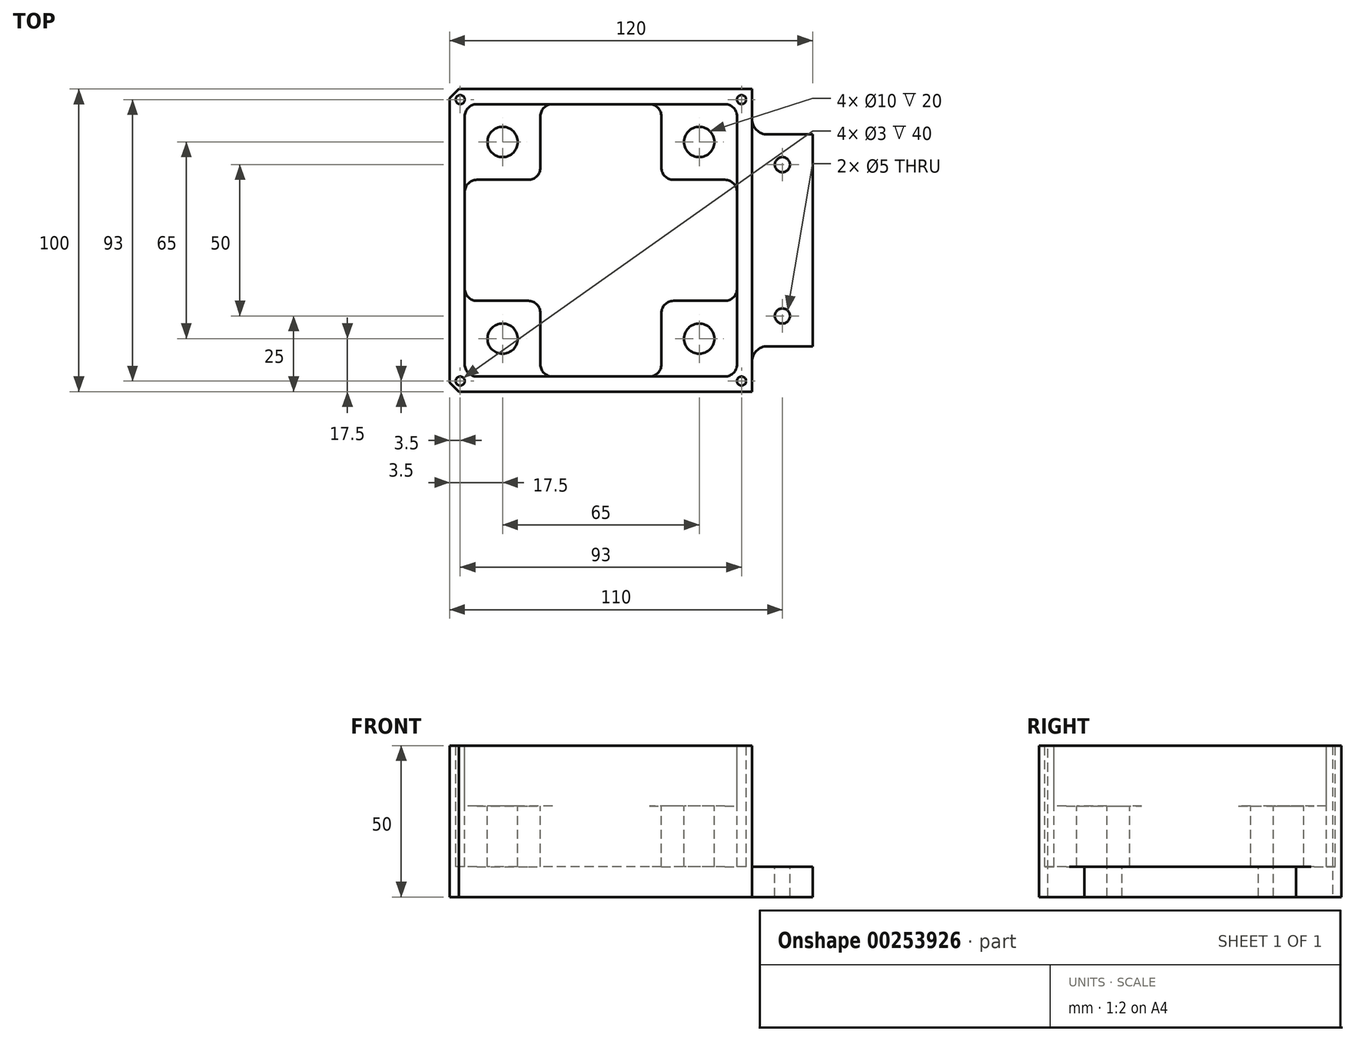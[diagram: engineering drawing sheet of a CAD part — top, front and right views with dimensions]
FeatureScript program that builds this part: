
annotation { "Feature Type Name" : "Feature", "Feature Type Description" : "" }
export const myFeature = defineFeature(function(context is Context, id is Id, definition is map)
    precondition{}
    {
        {
            var Q0;
            Q0=qCreatedBy(makeId("Top.planeOp"),FACE);
            var sketch = newSketch(context, id + "F0", { "sketchPlane" : qUnion([Q0])});
            skLineSegment(sketch, "E0.bottom", {"start": v(50, -50) * mm, "end": v(-50, -50) * mm});
            skLineSegment(sketch, "E0.top", {"start": v(50, 50) * mm, "end": v(-50, 50) * mm});
            skLineSegment(sketch, "E0.right", {"start": v(-50, -50) * mm, "end": v(-50, 50) * mm});
            skPoint(sketch, "E0.middle", {"position": v(0, 0) * mm});
            skLineSegment(sketch, "E1", {"start": v(50, 50) * mm, "end": v(70, 50) * mm});
            skLineSegment(sketch, "E2", {"start": v(70, 50) * mm, "end": v(70, -50) * mm});
            skLineSegment(sketch, "E3", {"start": v(70, -50) * mm, "end": v(50, -50) * mm});
            skSolve(sketch);
        }
        {
            var Q0;
            Q0=makeQuery(id+"F0.imprint","IMPRINT",FACE,{"disambiguationData":[TD([[makeQuery(id+"F0.imprint","IMPRINT",EDGE,{"derivedFrom":sQuery(id+"F0.wireOp",EDGE,"E0.bottom")}),-1.0]])]});
            extrude(context, id + "F1", {"entities" : qUnion([Q0]), "depth" : 50 * mm});
        }
        {
            var Q0;
            Q0=makeQuery(id+"F1.opExtrude","CAP_FACE",FACE,{"disambiguationData":[OSD([sQuery(id+"F0.wireOp",EDGE,"E0.bottom"),sQuery(id+"F0.wireOp",EDGE,"E0.top"),sQuery(id+"F0.wireOp",EDGE,"E0.right"),sQuery(id+"F0.wireOp",EDGE,"E1"),sQuery(id+"F0.wireOp",EDGE,"E2"),sQuery(id+"F0.wireOp",EDGE,"E3")])],"isStart":false});
            var sketch = newSketch(context, id + "F2", { "sketchPlane" : qUnion([Q0])});
            skLineSegment(sketch, "E4.bottom", {"start": v(70, 50) * mm, "end": v(50, 50) * mm});
            skLineSegment(sketch, "E4.top", {"start": v(70, -50) * mm, "end": v(50, -50) * mm});
            skLineSegment(sketch, "E4.left", {"start": v(70, 50) * mm, "end": v(70, -50) * mm});
            skLineSegment(sketch, "E4.right", {"start": v(50, 50) * mm, "end": v(50, -50) * mm});
            skSolve(sketch);
        }
        {
            var Q0;
            Q0=qSketchRegion(id+"F2",true);
            extrude(context, id + "F3", {"entities" : qUnion([Q0]), "operationType" : NewBodyOperationType.REMOVE, "oppositeDirection" : true, "depth" : 40 * mm});
        }
        {
            var Q0;
            Q0=makeQuery(id+"F3.boolean.opBoolean","COPY",FACE,{"derivedFrom":makeQuery(id+"F3.opExtrude","CAP_FACE",FACE,{"disambiguationData":[OSD([sQuery(id+"F2.wireOp",EDGE,"E4.bottom"),sQuery(id+"F2.wireOp",EDGE,"E4.top"),sQuery(id+"F2.wireOp",EDGE,"E4.left"),sQuery(id+"F2.wireOp",EDGE,"E4.right")])],"isStart":false})});
            var sketch = newSketch(context, id + "F4", { "sketchPlane" : qUnion([Q0])});
            skLineSegment(sketch, "E5.bottom", {"start": v(50, -50) * mm, "end": v(70, -50) * mm});
            skLineSegment(sketch, "E5.top", {"start": v(55, -35) * mm, "end": v(70, -35) * mm});
            skLineSegment(sketch, "E5.left", {"start": v(50, -50) * mm, "end": v(50, -40) * mm});
            skLineSegment(sketch, "E5.right", {"start": v(70, -50) * mm, "end": v(70, -35) * mm});
            skPoint(sketch, "E6.visualSharp", {"position": v(50, -35) * mm});
            skArc(sketch, "E6.filletArc", {"start": v(55, -35) * mm, "mid": v(51.46, -36.46) * mm, "end": v(50, -40) * mm});
            skCircle(sketch, "E7", {"center": v(60, -25) * mm, "radius": 2.5 * mm});
            skPoint(sketch, "E8.MirrorP", {"position": v(50, 35) * mm});
            skCircle(sketch, "E9.MirrorC", {"center": v(60, 25) * mm, "radius": 2.5 * mm});
            skArc(sketch, "E10.MirrorCS", {"start": v(55, 35) * mm, "mid": v(51.46, 36.46) * mm, "end": v(50, 40) * mm});
            skLineSegment(sketch, "E11.MirrorCS", {"start": v(70, 50) * mm, "end": v(70, 35) * mm});
            skLineSegment(sketch, "E12.MirrorCS", {"start": v(50, 50) * mm, "end": v(50, 40) * mm});
            skLineSegment(sketch, "E13.MirrorCS", {"start": v(50, 50) * mm, "end": v(70, 50) * mm});
            skLineSegment(sketch, "E14.MirrorCS", {"start": v(55, 35) * mm, "end": v(70, 35) * mm});
            skSolve(sketch);
        }
        {
            var Q0;
            Q0=qSketchRegion(id+"F4",true);
            extrude(context, id + "F5", {"entities" : qUnion([Q0]), "operationType" : NewBodyOperationType.REMOVE, "endBound" : BoundingType.UP_TO_NEXT, "oppositeDirection" : true, "depth" : 25 * mm});
        }
        {
            var Q0;
            Q0=makeQuery(id+"F1.opExtrude","CAP_FACE",FACE,{"disambiguationData":[OSD([sQuery(id+"F0.wireOp",EDGE,"E0.bottom"),sQuery(id+"F0.wireOp",EDGE,"E0.top"),sQuery(id+"F0.wireOp",EDGE,"E0.right"),sQuery(id+"F0.wireOp",EDGE,"E1"),sQuery(id+"F0.wireOp",EDGE,"E2"),sQuery(id+"F0.wireOp",EDGE,"E3")])],"isStart":false});
            var sketch = newSketch(context, id + "F6", { "sketchPlane" : qUnion([Q0])});
            skLineSegment(sketch, "E15.bottom", {"start": v(45, -45) * mm, "end": v(-45, -45) * mm});
            skLineSegment(sketch, "E15.top", {"start": v(45, 45) * mm, "end": v(-45, 45) * mm});
            skLineSegment(sketch, "E15.left", {"start": v(45, -45) * mm, "end": v(45, 45) * mm});
            skLineSegment(sketch, "E15.right", {"start": v(-45, -45) * mm, "end": v(-45, 45) * mm});
            skPoint(sketch, "E15.middle", {"position": v(0, 0) * mm});
            skSolve(sketch);
        }
        {
            var Q0;
            Q0=qSketchRegion(id+"F6",true);
            extrude(context, id + "F7", {"entities" : qUnion([Q0]), "operationType" : NewBodyOperationType.REMOVE, "oppositeDirection" : true, "depth" : 20 * mm});
        }
        {
            var Q0;
            Q0=makeQuery(id+"F7.boolean.opBoolean","COPY",FACE,{"derivedFrom":makeQuery(id+"F7.opExtrude","CAP_FACE",FACE,{"disambiguationData":[OSD([sQuery(id+"F6.wireOp",EDGE,"E15.bottom"),sQuery(id+"F6.wireOp",EDGE,"E15.top"),sQuery(id+"F6.wireOp",EDGE,"E15.left"),sQuery(id+"F6.wireOp",EDGE,"E15.right")])],"isStart":false})});
            var sketch = newSketch(context, id + "F8", { "sketchPlane" : qUnion([Q0])});
            skCircle(sketch, "E16", {"center": v(-32.5, 32.5) * mm, "radius": 5 * mm});
            skLineSegment(sketch, "E17.0", {"start": v(-45, -20) * mm, "end": v(-20, -20) * mm});
            skLineSegment(sketch, "E17.1", {"start": v(20, 45) * mm, "end": v(20, 20) * mm});
            skLineSegment(sketch, "E17.2", {"start": v(-20, 45) * mm, "end": v(20, 45) * mm});
            skLineSegment(sketch, "E17.3", {"start": v(-20, 45) * mm, "end": v(-20, 20) * mm});
            skLineSegment(sketch, "E17.4", {"start": v(-45, 20) * mm, "end": v(-20, 20) * mm});
            skLineSegment(sketch, "E17.5", {"start": v(45, 20) * mm, "end": v(20, 20) * mm});
            skLineSegment(sketch, "E17.6", {"start": v(-45, -20) * mm, "end": v(-45, 20) * mm});
            skLineSegment(sketch, "E17.7", {"start": v(45, 20) * mm, "end": v(45, -20) * mm});
            skLineSegment(sketch, "E17.8", {"start": v(45, -20) * mm, "end": v(20, -20) * mm});
            skLineSegment(sketch, "E17.9", {"start": v(20, -45) * mm, "end": v(20, -20) * mm});
            skLineSegment(sketch, "E17.10", {"start": v(20, -45) * mm, "end": v(-20, -45) * mm});
            skLineSegment(sketch, "E17.11", {"start": v(-20, -45) * mm, "end": v(-20, -20) * mm});
            skCircle(sketch, "E18.MirrorC", {"center": v(-32.5, -32.5) * mm, "radius": 5 * mm});
            skCircle(sketch, "E19.MirrorC", {"center": v(32.5, 32.5) * mm, "radius": 5 * mm});
            skCircle(sketch, "E20.MirrorC", {"center": v(32.5, -32.5) * mm, "radius": 5 * mm});
            skSolve(sketch);
        }
        {
            var Q0;
            Q0=qSketchRegion(id+"F8",true);
            extrude(context, id + "F9", {"entities" : qUnion([Q0]), "operationType" : NewBodyOperationType.REMOVE, "oppositeDirection" : true, "depth" : 20 * mm});
        }
        {
            var Q0;
            Q0=makeQuery(id+"F1.opExtrude","CAP_FACE",FACE,{"disambiguationData":[OSD([sQuery(id+"F0.wireOp",EDGE,"E0.bottom"),sQuery(id+"F0.wireOp",EDGE,"E0.top"),sQuery(id+"F0.wireOp",EDGE,"E0.right"),sQuery(id+"F0.wireOp",EDGE,"E1"),sQuery(id+"F0.wireOp",EDGE,"E2"),sQuery(id+"F0.wireOp",EDGE,"E3")])],"isStart":false});
            var sketch = newSketch(context, id + "F10", { "sketchPlane" : qUnion([Q0])});
            skCircle(sketch, "E21", {"center": v(-46.5, 46.5) * mm, "radius": 1.5 * mm});
            skCircle(sketch, "E22.MirrorC", {"center": v(-46.5, -46.5) * mm, "radius": 1.5 * mm});
            skCircle(sketch, "E23.MirrorC", {"center": v(46.5, 46.5) * mm, "radius": 1.5 * mm});
            skCircle(sketch, "E24.MirrorC", {"center": v(46.5, -46.5) * mm, "radius": 1.5 * mm});
            skSolve(sketch);
        }
        {
            var Q0;
            Q0=qSketchRegion(id+"F10",true);
            extrude(context, id + "F11", {"entities" : qUnion([Q0]), "operationType" : NewBodyOperationType.REMOVE, "oppositeDirection" : true, "depth" : 40 * mm});
        }
        {
            var Q0;
            Q0=makeQuery(id+"F5.boolean.opBoolean","COPY",EDGE,{"derivedFrom":makeQuery(id+"F5.opExtrude","SWEPT_EDGE",EDGE,{"disambiguationData":[OSD([sQuery(id+"F2.wireOp",EDGE,"E4.left"),sQuery(id+"F4.wireOp",EDGE,"E5.top"),sQuery(id+"F4.wireOp",EDGE,"E5.right")])]})});
            var Q1;
            Q1=makeQuery(id+"F5.boolean.opBoolean","COPY",EDGE,{"derivedFrom":makeQuery(id+"F5.opExtrude","SWEPT_EDGE",EDGE,{"disambiguationData":[OSD([sQuery(id+"F2.wireOp",EDGE,"E4.left"),sQuery(id+"F4.wireOp",EDGE,"E11.MirrorCS"),sQuery(id+"F4.wireOp",EDGE,"E14.MirrorCS")])]})});
            var Q2;
            {var subQ0=sQuery(id+"F2.wireOp",EDGE,"E4.right");var subQ1=sQuery(id+"F2.wireOp",EDGE,"E4.top");var subQ2=sQuery(id+"F0.wireOp",EDGE,"E3");var subQ3=sQuery(id+"F0.wireOp",EDGE,"E0.bottom");Q2=makeQuery(id+"F5.boolean.opBoolean","MERGE",EDGE,{"derivedFrom":[makeQuery(id+"F3.boolean.opBoolean","COPY",EDGE,{"derivedFrom":makeQuery(id+"F3.opExtrude","SWEPT_EDGE",EDGE,{"disambiguationData":[OSD([subQ3,subQ2,subQ1,subQ0])]})}),makeQuery(id+"F5.opExtrude","SWEPT_EDGE",EDGE,{"disambiguationData":[OSD([subQ3,subQ2,subQ1,subQ0,sQuery(id+"F4.wireOp",EDGE,"E5.bottom"),sQuery(id+"F4.wireOp",EDGE,"E5.left")])]})]});}
            var Q3;
            Q3=makeQuery(id+"F1.opExtrude","SWEPT_EDGE",EDGE,{"disambiguationData":[OSD([sQuery(id+"F0.wireOp",EDGE,"E0.bottom"),sQuery(id+"F0.wireOp",EDGE,"E0.right")])]});
            var Q4;
            {var subQ0=sQuery(id+"F2.wireOp",EDGE,"E4.right");var subQ1=sQuery(id+"F2.wireOp",EDGE,"E4.bottom");var subQ2=sQuery(id+"F0.wireOp",EDGE,"E1");var subQ3=sQuery(id+"F0.wireOp",EDGE,"E0.top");Q4=makeQuery(id+"F5.boolean.opBoolean","MERGE",EDGE,{"derivedFrom":[makeQuery(id+"F3.boolean.opBoolean","COPY",EDGE,{"derivedFrom":makeQuery(id+"F3.opExtrude","SWEPT_EDGE",EDGE,{"disambiguationData":[OSD([subQ3,subQ2,subQ1,subQ0])]})}),makeQuery(id+"F5.opExtrude","SWEPT_EDGE",EDGE,{"disambiguationData":[OSD([subQ3,subQ2,subQ1,subQ0,sQuery(id+"F4.wireOp",EDGE,"E12.MirrorCS"),sQuery(id+"F4.wireOp",EDGE,"E13.MirrorCS")])]})]});}
            var Q5;
            Q5=makeQuery(id+"F1.opExtrude","SWEPT_EDGE",EDGE,{"disambiguationData":[OSD([sQuery(id+"F0.wireOp",EDGE,"E0.top"),sQuery(id+"F0.wireOp",EDGE,"E0.right")])]});
            chamfer(context, id + "F12", {"entities" : qUnion([Q0, Q1, Q2, Q3, Q4, Q5]), "width" : 3 * mm, "tangentPropagation" : true});
        }
        {
            var Q0;
            Q0=makeQuery(id+"F7.boolean.opBoolean","COPY",EDGE,{"derivedFrom":makeQuery(id+"F7.opExtrude","SWEPT_EDGE",EDGE,{"disambiguationData":[OSD([sQuery(id+"F6.wireOp",EDGE,"E15.top"),sQuery(id+"F6.wireOp",EDGE,"E15.right")])]})});
            var Q1;
            Q1=makeQuery(id+"F7.boolean.opBoolean","COPY",EDGE,{"derivedFrom":makeQuery(id+"F7.opExtrude","SWEPT_EDGE",EDGE,{"disambiguationData":[OSD([sQuery(id+"F6.wireOp",EDGE,"E15.top"),sQuery(id+"F6.wireOp",EDGE,"E15.left")])]})});
            var Q2;
            Q2=makeQuery(id+"F7.boolean.opBoolean","COPY",EDGE,{"derivedFrom":makeQuery(id+"F7.opExtrude","SWEPT_EDGE",EDGE,{"disambiguationData":[OSD([sQuery(id+"F6.wireOp",EDGE,"E15.bottom"),sQuery(id+"F6.wireOp",EDGE,"E15.left")])]})});
            var Q3;
            Q3=makeQuery(id+"F7.boolean.opBoolean","COPY",EDGE,{"derivedFrom":makeQuery(id+"F7.opExtrude","SWEPT_EDGE",EDGE,{"disambiguationData":[OSD([sQuery(id+"F6.wireOp",EDGE,"E15.bottom"),sQuery(id+"F6.wireOp",EDGE,"E15.right")])]})});
            var Q4;
            Q4=makeQuery(id+"F9.boolean.opBoolean","COPY",EDGE,{"derivedFrom":makeQuery(id+"F9.opExtrude","SWEPT_EDGE",EDGE,{"disambiguationData":[OSD([sQuery(id+"F6.wireOp",EDGE,"E15.right"),sQuery(id+"F8.wireOp",EDGE,"E17.4"),sQuery(id+"F8.wireOp",EDGE,"E17.6")])]})});
            var Q5;
            Q5=makeQuery(id+"F9.boolean.opBoolean","COPY",EDGE,{"derivedFrom":makeQuery(id+"F9.opExtrude","SWEPT_EDGE",EDGE,{"disambiguationData":[OSD([sQuery(id+"F8.wireOp",EDGE,"E17.3"),sQuery(id+"F8.wireOp",EDGE,"E17.4")])]})});
            var Q6;
            Q6=makeQuery(id+"F9.boolean.opBoolean","COPY",EDGE,{"derivedFrom":makeQuery(id+"F9.opExtrude","SWEPT_EDGE",EDGE,{"disambiguationData":[OSD([sQuery(id+"F6.wireOp",EDGE,"E15.top"),sQuery(id+"F8.wireOp",EDGE,"E17.2"),sQuery(id+"F8.wireOp",EDGE,"E17.3")])]})});
            var Q7;
            Q7=makeQuery(id+"F9.boolean.opBoolean","COPY",EDGE,{"derivedFrom":makeQuery(id+"F9.opExtrude","SWEPT_EDGE",EDGE,{"disambiguationData":[OSD([sQuery(id+"F6.wireOp",EDGE,"E15.top"),sQuery(id+"F8.wireOp",EDGE,"E17.1"),sQuery(id+"F8.wireOp",EDGE,"E17.2")])]})});
            var Q8;
            Q8=makeQuery(id+"F9.boolean.opBoolean","COPY",EDGE,{"derivedFrom":makeQuery(id+"F9.opExtrude","SWEPT_EDGE",EDGE,{"disambiguationData":[OSD([sQuery(id+"F8.wireOp",EDGE,"E17.1"),sQuery(id+"F8.wireOp",EDGE,"E17.5")])]})});
            var Q9;
            Q9=makeQuery(id+"F9.boolean.opBoolean","COPY",EDGE,{"derivedFrom":makeQuery(id+"F9.opExtrude","SWEPT_EDGE",EDGE,{"disambiguationData":[OSD([sQuery(id+"F6.wireOp",EDGE,"E15.left"),sQuery(id+"F8.wireOp",EDGE,"E17.5"),sQuery(id+"F8.wireOp",EDGE,"E17.7")])]})});
            var Q10;
            Q10=makeQuery(id+"F9.boolean.opBoolean","COPY",EDGE,{"derivedFrom":makeQuery(id+"F9.opExtrude","SWEPT_EDGE",EDGE,{"disambiguationData":[OSD([sQuery(id+"F6.wireOp",EDGE,"E15.right"),sQuery(id+"F8.wireOp",EDGE,"E17.0"),sQuery(id+"F8.wireOp",EDGE,"E17.6")])]})});
            var Q11;
            Q11=makeQuery(id+"F9.boolean.opBoolean","COPY",EDGE,{"derivedFrom":makeQuery(id+"F9.opExtrude","SWEPT_EDGE",EDGE,{"disambiguationData":[OSD([sQuery(id+"F8.wireOp",EDGE,"E17.0"),sQuery(id+"F8.wireOp",EDGE,"E17.11")])]})});
            var Q12;
            Q12=makeQuery(id+"F9.boolean.opBoolean","COPY",EDGE,{"derivedFrom":makeQuery(id+"F9.opExtrude","SWEPT_EDGE",EDGE,{"disambiguationData":[OSD([sQuery(id+"F6.wireOp",EDGE,"E15.bottom"),sQuery(id+"F8.wireOp",EDGE,"E17.10"),sQuery(id+"F8.wireOp",EDGE,"E17.11")])]})});
            var Q13;
            Q13=makeQuery(id+"F9.boolean.opBoolean","COPY",EDGE,{"derivedFrom":makeQuery(id+"F9.opExtrude","SWEPT_EDGE",EDGE,{"disambiguationData":[OSD([sQuery(id+"F6.wireOp",EDGE,"E15.bottom"),sQuery(id+"F8.wireOp",EDGE,"E17.9"),sQuery(id+"F8.wireOp",EDGE,"E17.10")])]})});
            var Q14;
            Q14=makeQuery(id+"F9.boolean.opBoolean","COPY",EDGE,{"derivedFrom":makeQuery(id+"F9.opExtrude","SWEPT_EDGE",EDGE,{"disambiguationData":[OSD([sQuery(id+"F8.wireOp",EDGE,"E17.8"),sQuery(id+"F8.wireOp",EDGE,"E17.9")])]})});
            var Q15;
            Q15=makeQuery(id+"F9.boolean.opBoolean","COPY",EDGE,{"derivedFrom":makeQuery(id+"F9.opExtrude","SWEPT_EDGE",EDGE,{"disambiguationData":[OSD([sQuery(id+"F6.wireOp",EDGE,"E15.left"),sQuery(id+"F8.wireOp",EDGE,"E17.7"),sQuery(id+"F8.wireOp",EDGE,"E17.8")])]})});
            fillet(context, id + "F13", {"entities" : qUnion([Q0, Q1, Q2, Q3, Q4, Q5, Q6, Q7, Q8, Q9, Q10, Q11, Q12, Q13, Q14, Q15]), "radius" : 4 * mm, "tangentPropagation" : true, "allowEdgeOverflow" : false});
        }
    });
